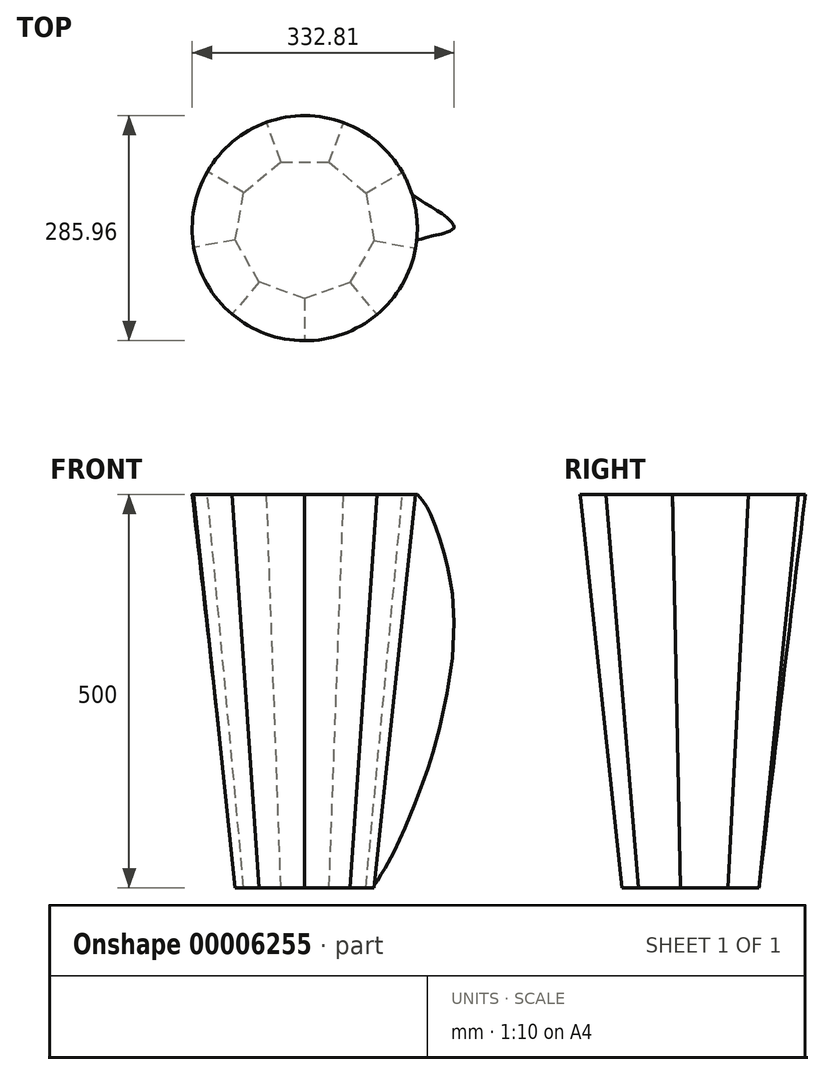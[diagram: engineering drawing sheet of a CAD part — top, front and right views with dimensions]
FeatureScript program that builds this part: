
annotation { "Feature Type Name" : "Feature", "Feature Type Description" : "" }
export const myFeature = defineFeature(function(context is Context, id is Id, definition is map)
    precondition{}
    {
        {
            var Q0;
            Q0=qCreatedBy(makeId("Top.planeOp"),FACE);
            var sketch = newSketch(context, id + "F0", { "sketchPlane" : qUnion([Q0])});
            skCircle(sketch, "E0.cCircle", {"center": v(0, 0) * mm, "radius": 84.18 * mm, "construction": true});
            skLineSegment(sketch, "E0.0", {"start": v(-57.84, -68.4) * mm, "end": v(-88.28, -15.22) * mm});
            skLineSegment(sketch, "E0.1", {"start": v(-88.28, -15.22) * mm, "end": v(-77.4, 45.09) * mm});
            skLineSegment(sketch, "E0.2", {"start": v(-77.4, 45.09) * mm, "end": v(-30.32, 84.3) * mm});
            skLineSegment(sketch, "E0.3", {"start": v(-30.32, 84.3) * mm, "end": v(30.96, 84.06) * mm});
            skLineSegment(sketch, "E0.4", {"start": v(30.96, 84.06) * mm, "end": v(77.75, 44.5) * mm});
            skLineSegment(sketch, "E0.5", {"start": v(77.75, 44.5) * mm, "end": v(88.16, -15.9) * mm});
            skLineSegment(sketch, "E0.6", {"start": v(88.16, -15.9) * mm, "end": v(57.32, -68.84) * mm});
            skLineSegment(sketch, "E0.7", {"start": v(57.32, -68.84) * mm, "end": v(-0.34, -89.58) * mm});
            skLineSegment(sketch, "E0.8", {"start": v(-0.34, -89.58) * mm, "end": v(-57.84, -68.4) * mm});
            skPoint(sketch, "E0.0.midPoint", {"position": v(-73.06, -41.81) * mm});
            skSolve(sketch);
        }
        {
            var Q0;
            Q0=qCreatedBy(makeId("Top.planeOp"),FACE);
            cPlane(context, id + "F1", {"entities" : qUnion([Q0]), "cplaneType" : CPlaneType.OFFSET, "offset" : 500 * mm, "width" : 150 * mm, "height" : 150 * mm});
        }
        {
            var Q0;
            Q0=qCreatedBy(id+"F1.planeOp",FACE);
            var sketch = newSketch(context, id + "F2", { "sketchPlane" : qUnion([Q0])});
            skLineSegment(sketch, "E1", {"start": v(0, 0) * mm, "end": v(49.43, 134.16) * mm, "construction": true});
            skLineSegment(sketch, "E2.1.0", {"start": v(0, 0) * mm, "end": v(-48.37, 134.55) * mm, "construction": true});
            skLineSegment(sketch, "E2.2.0", {"start": v(0, 0) * mm, "end": v(-123.54, 71.98) * mm, "construction": true});
            skPoint(sketch, "E2.center", {"position": v(0, 0) * mm});
            skLineSegment(sketch, "E3.1.3.0", {"start": v(0, 0) * mm, "end": v(-140.9, -24.27) * mm, "construction": true});
            skLineSegment(sketch, "E3.1.4.0", {"start": v(0, 0) * mm, "end": v(-92.34, -109.17) * mm, "construction": true});
            skLineSegment(sketch, "E3.1.5.0", {"start": v(0, 0) * mm, "end": v(-0.57, -142.98) * mm, "construction": true});
            skLineSegment(sketch, "E3.1.6.0", {"start": v(0, 0) * mm, "end": v(91.47, -109.9) * mm, "construction": true});
            skLineSegment(sketch, "E3.1.7.0", {"start": v(0, 0) * mm, "end": v(140.71, -25.39) * mm, "construction": true});
            skLineSegment(sketch, "E3.1.8.0", {"start": v(0, 0) * mm, "end": v(124.1, 71) * mm, "construction": true});
            skArc(sketch, "E4", {"start": v(-48.37, 134.55) * mm, "mid": v(-91.47, 109.9) * mm, "end": v(-123.54, 71.98) * mm});
            skArc(sketch, "E5", {"start": v(49.43, 134.16) * mm, "mid": v(0.57, 142.98) * mm, "end": v(-48.37, 134.55) * mm});
            skArc(sketch, "E6", {"start": v(124.1, 71) * mm, "mid": v(92.34, 109.17) * mm, "end": v(49.43, 134.16) * mm});
            skArc(sketch, "E7", {"start": v(140.71, -25.39) * mm, "mid": v(140.9, 24.27) * mm, "end": v(124.1, 71) * mm});
            skArc(sketch, "E8", {"start": v(91.47, -109.9) * mm, "mid": v(123.54, -71.98) * mm, "end": v(140.71, -25.39) * mm});
            skArc(sketch, "E9", {"start": v(-0.57, -142.98) * mm, "mid": v(48.37, -134.55) * mm, "end": v(91.47, -109.9) * mm});
            skArc(sketch, "E10", {"start": v(-92.34, -109.17) * mm, "mid": v(-49.43, -134.16) * mm, "end": v(-0.57, -142.98) * mm});
            skArc(sketch, "E11", {"start": v(-140.9, -24.27) * mm, "mid": v(-124.1, -71) * mm, "end": v(-92.34, -109.17) * mm});
            skArc(sketch, "E12", {"start": v(-123.54, 71.98) * mm, "mid": v(-140.71, 25.39) * mm, "end": v(-140.9, -24.27) * mm});
            skLineSegment(sketch, "E13", {"start": v(-48.37, 134.55) * mm, "end": v(-48.37, 134.55) * mm});
            skSolve(sketch);
        }
        {
            var Q0;
            Q0=qCreatedBy(makeId("Front.planeOp"),FACE);
            var sketch = newSketch(context, id + "F3", { "sketchPlane" : qUnion([Q0])});
            skFitSpline(sketch, "E14", {"points": [v(85.42, 0) * mm, v(146.04, 122.7) * mm, v(177.14, 228.46) * mm, v(187.9, 369.57) * mm, v(155.64, 482.94) * mm, v(142.98, 500) * mm], "startDerivative": vector(282.36, 360.15) * mm, "endDerivative": vector(-127.08, 130.35) * mm});
            skSolve(sketch);
        }
        {
            var Q0;
            Q0=makeQuery(id+"F0.imprint","IMPRINT",FACE,{"disambiguationData":[TD([[makeQuery(id+"F0.imprint","IMPRINT",EDGE,{"derivedFrom":sQuery(id+"F0.wireOp",EDGE,"E0.0")}),-1.0]])]});
            var Q1;
            Q1=makeQuery(id+"F2.imprint","IMPRINT",FACE,{"disambiguationData":[TD([[makeQuery(id+"F2.imprint","IMPRINT",EDGE,{"derivedFrom":sQuery(id+"F2.wireOp",EDGE,"E4")}),1.0]])]});
            var Q2;
            Q2=sQuery(id+"F3.wireOp",EDGE,"E14");
            loft(context, id + "F4", {"addGuides" : true, "sheetProfilesArray" : [{ "sheetProfileEntities" : qUnion([Q0]) }, { "sheetProfileEntities" : qUnion([Q1]) }], "guidesArray" : [{ "guideEntities" : qUnion([Q2]), "guideDerivativeType" : LoftGuideDerivativeType.DEFAULT, "guideDerivativeMagnitude" : 1 }]});
        }
    });
